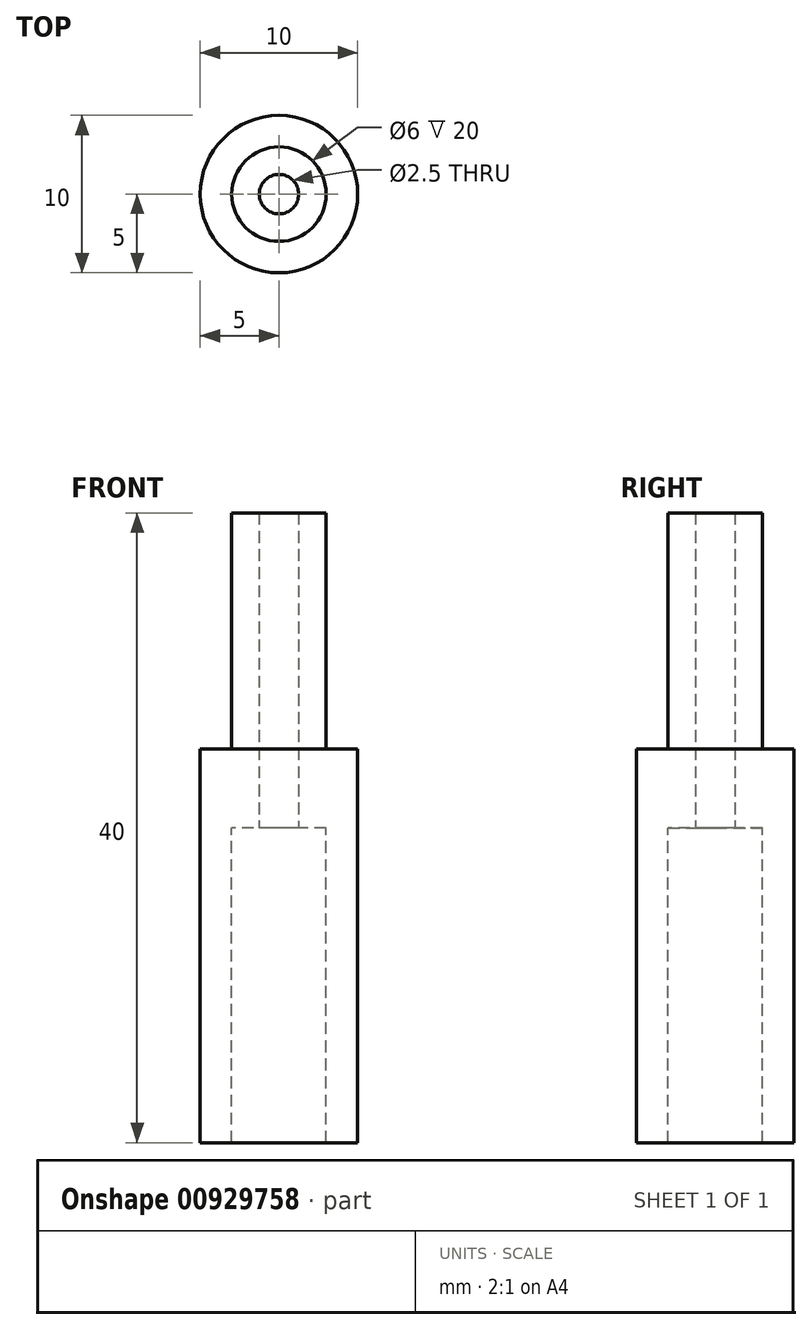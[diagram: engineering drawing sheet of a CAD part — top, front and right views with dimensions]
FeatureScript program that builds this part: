
annotation { "Feature Type Name" : "Feature", "Feature Type Description" : "" }
export const myFeature = defineFeature(function(context is Context, id is Id, definition is map)
    precondition{}
    {
        {
            var Q0;
            Q0=qCreatedBy(makeId("Top.planeOp"),FACE);
            var sketch = newSketch(context, id + "F0", { "sketchPlane" : qUnion([Q0])});
            skCircle(sketch, "E0", {"center": v(0, 0) * mm, "radius": 3 * mm});
            skCircle(sketch, "E1", {"center": v(0, 0) * mm, "radius": 5 * mm});
            skCircle(sketch, "E2", {"center": v(0, 0) * mm, "radius": 1.25 * mm});
            skSolve(sketch);
        }
        {
            var Q0;
            Q0=makeQuery(id+"F0.imprint","IMPRINT",FACE,{"disambiguationData":[TD([[makeQuery(id+"F0.imprint","IMPRINT",EDGE,{"derivedFrom":sQuery(id+"F0.wireOp",EDGE,"E0")}),-1.0]])]});
            extrude(context, id + "F1", {"entities" : qUnion([Q0]), "oppositeDirection" : true, "depth" : 25 * mm, "offsetDistance" : 25 * mm});
        }
        {
            var Q0;
            Q0=makeQuery(id+"F0.imprint","IMPRINT",FACE,{"disambiguationData":[TD([[makeQuery(id+"F0.imprint","IMPRINT",EDGE,{"derivedFrom":sQuery(id+"F0.wireOp",EDGE,"E0")}),1.0]])]});
            extrude(context, id + "F2", {"entities" : qUnion([Q0]), "operationType" : NewBodyOperationType.ADD, "depth" : 15 * mm, "offsetDistance" : 25 * mm, "hasSecondDirection" : true, "secondDirectionOppositeDirection" : true, "secondDirectionDepth" : 5 * mm});
        }
    });
